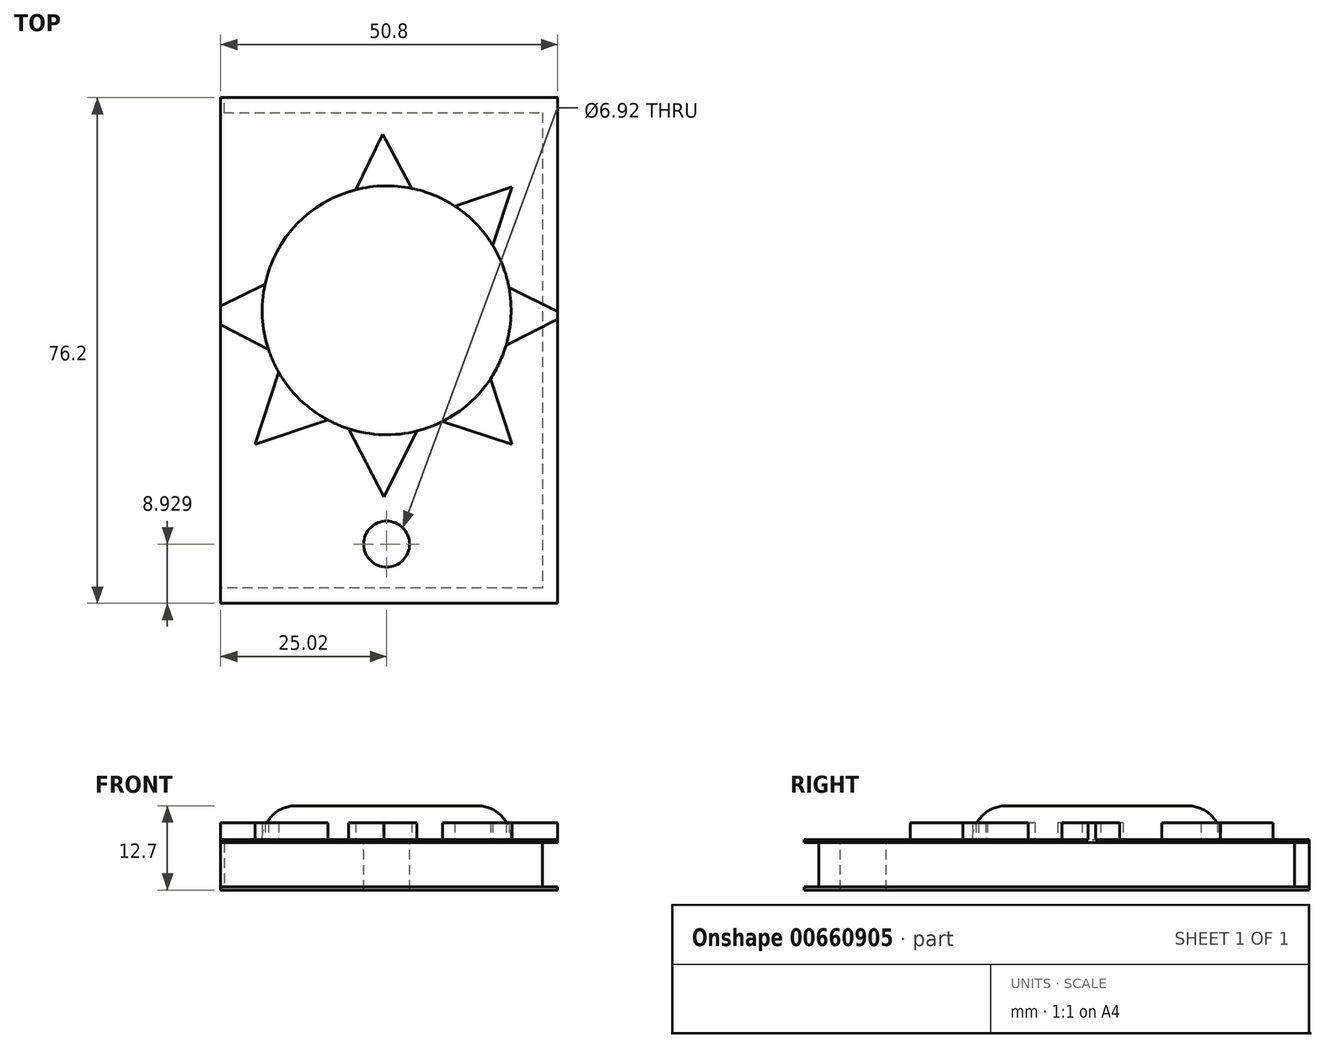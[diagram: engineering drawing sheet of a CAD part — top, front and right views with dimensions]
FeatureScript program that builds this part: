
annotation { "Feature Type Name" : "Feature", "Feature Type Description" : "" }
export const myFeature = defineFeature(function(context is Context, id is Id, definition is map)
    precondition{}
    {
        {
            var Q0;
            Q0=qCreatedBy(makeId("Top.planeOp"),FACE);
            var sketch = newSketch(context, id + "F0", { "sketchPlane" : qUnion([Q0])});
            skLineSegment(sketch, "E0.bottom", {"start": v(-25.02, 32.04) * mm, "end": v(25.78, 32.04) * mm});
            skLineSegment(sketch, "E0.top", {"start": v(-25.02, -44.16) * mm, "end": v(25.78, -44.16) * mm});
            skLineSegment(sketch, "E0.left", {"start": v(-25.02, 32.04) * mm, "end": v(-25.02, -44.16) * mm});
            skLineSegment(sketch, "E0.right", {"start": v(25.78, 32.04) * mm, "end": v(25.78, -44.16) * mm});
            skSolve(sketch);
        }
        {
            var Q0;
            Q0=makeQuery(id+"F0.imprint","IMPRINT",FACE,{"disambiguationData":[TD([[makeQuery(id+"F0.imprint","IMPRINT",EDGE,{"derivedFrom":sQuery(id+"F0.wireOp",EDGE,"E0.bottom")}),-1.0]])]});
            extrude(context, id + "F1", {"entities" : qUnion([Q0]), "depth" : 7.62 * mm, "offsetDistance" : 25.4 * mm});
        }
        {
            var Q0;
            Q0=makeQuery(id+"F1.opExtrude","CAP_FACE",FACE,{"disambiguationData":[OSD([sQuery(id+"F0.wireOp",EDGE,"E0.bottom"),sQuery(id+"F0.wireOp",EDGE,"E0.top"),sQuery(id+"F0.wireOp",EDGE,"E0.left"),sQuery(id+"F0.wireOp",EDGE,"E0.right")])],"isStart":false});
            var sketch = newSketch(context, id + "F2", { "sketchPlane" : qUnion([Q0])});
            skCircle(sketch, "E1", {"center": v(0, 0) * mm, "radius": 18.75 * mm});
            skSolve(sketch);
        }
        {
            var Q0;
            Q0=makeQuery(id+"F2.imprint","IMPRINT",FACE,{"disambiguationData":[TD([[makeQuery(id+"F2.imprint","IMPRINT",EDGE,{"derivedFrom":sQuery(id+"F2.wireOp",EDGE,"E1")}),1.0]])]});
            extrude(context, id + "F3", {"entities" : qUnion([Q0]), "operationType" : NewBodyOperationType.ADD, "depth" : 5.08 * mm, "offsetDistance" : 25.4 * mm});
        }
        {
            var Q0;
            Q0=makeQuery(id+"F3.opExtrude","CAP_EDGE",EDGE,{"disambiguationData":[OSD([sQuery(id+"F2.wireOp",EDGE,"E1")])],"isStart":false});
            fillet(context, id + "F4", {"entities" : qUnion([Q0]), "radius" : 5.08 * mm, "tangentPropagation" : true, "allowEdgeOverflow" : false});
        }
        {
            var Q0;
            Q0=makeQuery(id+"F1.opExtrude","CAP_FACE",FACE,{"disambiguationData":[OSD([sQuery(id+"F0.wireOp",EDGE,"E0.bottom"),sQuery(id+"F0.wireOp",EDGE,"E0.top"),sQuery(id+"F0.wireOp",EDGE,"E0.left"),sQuery(id+"F0.wireOp",EDGE,"E0.right")])],"isStart":false});
            var sketch = newSketch(context, id + "F5", { "sketchPlane" : qUnion([Q0])});
            skLineSegment(sketch, "E2", {"start": v(-16.56, 8.8) * mm, "end": v(-20, 18.6) * mm});
            skLineSegment(sketch, "E3", {"start": v(-20, 18.6) * mm, "end": v(-10.58, 15.49) * mm});
            skLineSegment(sketch, "E4", {"start": v(-10.58, 15.49) * mm, "end": v(-16.56, 8.8) * mm});
            skLineSegment(sketch, "E5", {"start": v(-4.65, 18.17) * mm, "end": v(-0.57, 26.55) * mm});
            skLineSegment(sketch, "E6", {"start": v(-0.57, 26.55) * mm, "end": v(3.77, 18.37) * mm});
            skLineSegment(sketch, "E7", {"start": v(3.77, 18.37) * mm, "end": v(-4.65, 18.17) * mm});
            skLineSegment(sketch, "E8", {"start": v(10.26, 15.7) * mm, "end": v(18.9, 18.59) * mm});
            skLineSegment(sketch, "E9", {"start": v(18.9, 18.59) * mm, "end": v(16, 9.77) * mm});
            skLineSegment(sketch, "E10", {"start": v(16, 9.77) * mm, "end": v(10.26, 15.7) * mm});
            skLineSegment(sketch, "E11", {"start": v(18.43, 3.45) * mm, "end": v(26.88, -0.76) * mm});
            skLineSegment(sketch, "E12", {"start": v(26.88, -0.76) * mm, "end": v(18, -5.29) * mm});
            skLineSegment(sketch, "E13", {"start": v(18, -5.29) * mm, "end": v(18.43, 3.45) * mm});
            skLineSegment(sketch, "E14", {"start": v(8.42, -16.75) * mm, "end": v(18.93, -20.19) * mm});
            skLineSegment(sketch, "E15", {"start": v(18.93, -20.19) * mm, "end": v(15.63, -10.36) * mm});
            skLineSegment(sketch, "E16", {"start": v(15.63, -10.36) * mm, "end": v(8.42, -16.75) * mm});
            skLineSegment(sketch, "E17", {"start": v(4.55, -18.2) * mm, "end": v(-0.38, -28.12) * mm});
            skLineSegment(sketch, "E18", {"start": v(-0.38, -28.12) * mm, "end": v(-5.71, -17.86) * mm});
            skLineSegment(sketch, "E19", {"start": v(-5.71, -17.86) * mm, "end": v(4.55, -18.2) * mm});
            skLineSegment(sketch, "E20", {"start": v(-8.85, -16.53) * mm, "end": v(-19.83, -20.21) * mm});
            skLineSegment(sketch, "E21", {"start": v(-19.83, -20.21) * mm, "end": v(-16.27, -9.32) * mm});
            skLineSegment(sketch, "E22", {"start": v(-16.27, -9.32) * mm, "end": v(-8.85, -16.53) * mm});
            skLineSegment(sketch, "E23", {"start": v(-18.34, 3.93) * mm, "end": v(-27.79, -0.78) * mm});
            skLineSegment(sketch, "E24", {"start": v(-27.79, -0.78) * mm, "end": v(-17.8, -5.9) * mm});
            skLineSegment(sketch, "E25", {"start": v(-17.8, -5.9) * mm, "end": v(-18.34, 3.93) * mm});
            skSolve(sketch);
        }
        {
            var Q0;
            {var subQ0=sQuery(id+"F5.wireOp",EDGE,"E2");Q0=makeQuery(id+"F5.imprint","IMPRINT",FACE,{"disambiguationData":[TD([[makeQuery(id+"F5.imprint","IMPRINT",EDGE,{"derivedFrom":subQ0}),-1.0]])]});}
            var sketch = newSketch(context, id + "F6", { "sketchPlane" : qUnion([Q0])});
            skSolve(sketch);
        }
        {
            var Q0;
            {var subQ1=sQuery(id+"F5.wireOp",EDGE,"E23");var subQ2=sQuery(id+"F0.wireOp",EDGE,"E0.left");var subQ5=makeQuery(id+"F1.opExtrude","CAP_EDGE",EDGE,{"disambiguationData":[OSD([subQ2])],"isStart":false});var subQ6=makeQuery(id+"F5.imprint","INTERSECT",VERTEX,{"derivedFrom":[subQ5,subQ1]});Q0=makeQuery(id+"F5.imprint","IMPRINT",FACE,{"disambiguationData":[TD([[makeQuery(id+"F5.imprint","IMPRINT",EDGE,{"disambiguationData":[TD([[subQ6,-1.0]])],"derivedFrom":subQ5}),1.0]])]});}
            var Q1;
            {var subQ0=sQuery(id+"F5.wireOp",EDGE,"E5");Q1=makeQuery(id+"F5.imprint","IMPRINT",FACE,{"disambiguationData":[TD([[makeQuery(id+"F5.imprint","IMPRINT",EDGE,{"derivedFrom":subQ0}),-1.0]])]});}
            var Q2;
            {var subQ0=sQuery(id+"F5.wireOp",EDGE,"E8");Q2=makeQuery(id+"F5.imprint","IMPRINT",FACE,{"disambiguationData":[TD([[makeQuery(id+"F5.imprint","IMPRINT",EDGE,{"derivedFrom":subQ0}),-1.0]])]});}
            var Q3;
            {var subQ1=sQuery(id+"F5.wireOp",EDGE,"E11");var subQ2=sQuery(id+"F0.wireOp",EDGE,"E0.right");var subQ5=makeQuery(id+"F1.opExtrude","CAP_EDGE",EDGE,{"disambiguationData":[OSD([subQ2])],"isStart":false});var subQ6=makeQuery(id+"F5.imprint","INTERSECT",VERTEX,{"derivedFrom":[subQ5,subQ1]});Q3=makeQuery(id+"F5.imprint","IMPRINT",FACE,{"disambiguationData":[TD([[makeQuery(id+"F5.imprint","IMPRINT",EDGE,{"disambiguationData":[TD([[subQ6,-1.0]])],"derivedFrom":subQ5}),-1.0]])]});}
            var Q4;
            {var subQ0=sQuery(id+"F5.wireOp",EDGE,"E14");Q4=makeQuery(id+"F5.imprint","IMPRINT",FACE,{"disambiguationData":[TD([[makeQuery(id+"F5.imprint","IMPRINT",EDGE,{"derivedFrom":subQ0}),1.0]])]});}
            var Q5;
            {var subQ0=sQuery(id+"F5.wireOp",EDGE,"E17");Q5=makeQuery(id+"F5.imprint","IMPRINT",FACE,{"disambiguationData":[TD([[makeQuery(id+"F5.imprint","IMPRINT",EDGE,{"derivedFrom":subQ0}),-1.0]])]});}
            var Q6;
            {var subQ0=sQuery(id+"F5.wireOp",EDGE,"E20");Q6=makeQuery(id+"F5.imprint","IMPRINT",FACE,{"disambiguationData":[TD([[makeQuery(id+"F5.imprint","IMPRINT",EDGE,{"derivedFrom":subQ0}),-1.0]])]});}
            var Q7;
            {var subQ0=sQuery(id+"F5.wireOp",EDGE,"E2");Q7=makeQuery(id+"F6.imprint","IMPRINT",FACE,{"disambiguationData":[TD([[makeQuery(id+"F6.imprint","IMPRINT",EDGE,{"derivedFrom":makeQuery(id+"F5.imprint","IMPRINT",EDGE,{"derivedFrom":subQ0})}),-1.0]])]});}
            extrude(context, id + "F7", {"entities" : qUnion([Q0, Q1, Q2, Q3, Q4, Q5, Q6, Q7]), "operationType" : NewBodyOperationType.ADD, "depth" : 2.54 * mm, "offsetDistance" : 25.4 * mm});
        }
        {
            var Q0;
            Q0=makeQuery(id+"F1.opExtrude","SWEPT_FACE",FACE,{"disambiguationData":[OSD([sQuery(id+"F0.wireOp",EDGE,"E0.bottom")])]});
            var sketch = newSketch(context, id + "F8", { "sketchPlane" : qUnion([Q0])});
            skLineSegment(sketch, "E26", {"start": v(24.5, 7.13) * mm, "end": v(-25.78, 7.13) * mm});
            skLineSegment(sketch, "E27", {"start": v(24.5, 0.48) * mm, "end": v(-25.78, 0.48) * mm});
            skLineSegment(sketch, "E28", {"start": v(24.5, 7.13) * mm, "end": v(24.5, 0.48) * mm});
            skPoint(sketch, "E29.orphan", {"position": v(25.02, 7.13) * mm});
            skPoint(sketch, "E30.orphan", {"position": v(25.02, 0.48) * mm});
            skSolve(sketch);
        }
        {
            var Q0;
            {var subQ0=sQuery(id+"F8.wireOp",EDGE,"E26");Q0=makeQuery(id+"F8.imprint","IMPRINT",FACE,{"disambiguationData":[TD([[makeQuery(id+"F8.imprint","IMPRINT",EDGE,{"derivedFrom":subQ0}),1.0]])]});}
            extrude(context, id + "F9", {"entities" : qUnion([Q0]), "operationType" : NewBodyOperationType.REMOVE, "oppositeDirection" : true, "depth" : 2.3 * mm, "offsetDistance" : 25.4 * mm});
        }
        {
            var Q0;
            {var subQ0=sQuery(id+"F0.wireOp",EDGE,"E0.right");Q0=makeQuery(id+"F7.boolean.opBoolean","MERGE",FACE,{"derivedFrom":[makeQuery(id+"F1.opExtrude","SWEPT_FACE",FACE,{"disambiguationData":[OSD([subQ0])]}),makeQuery(id+"F7.opExtrude","SWEPT_FACE",FACE,{"disambiguationData":[OSD([subQ0])]})]});}
            var sketch = newSketch(context, id + "F10", { "sketchPlane" : qUnion([Q0])});
            skLineSegment(sketch, "E31", {"start": v(29.76, 7.13) * mm, "end": v(-44.16, 7.13) * mm});
            skPoint(sketch, "E31.endSnap0", {"position": v(-44.16, 3.81) * mm});
            skLineSegment(sketch, "E32", {"start": v(29.76, 0.48) * mm, "end": v(-44.16, 0.48) * mm});
            skSolve(sketch);
        }
        {
            var Q0;
            {var subQ0=sQuery(id+"F10.wireOp",EDGE,"E31");Q0=makeQuery(id+"F10.imprint","IMPRINT",FACE,{"disambiguationData":[TD([[makeQuery(id+"F10.imprint","IMPRINT",EDGE,{"derivedFrom":subQ0}),1.0]])]});}
            extrude(context, id + "F11", {"entities" : qUnion([Q0]), "operationType" : NewBodyOperationType.REMOVE, "oppositeDirection" : true, "depth" : 2.3 * mm, "offsetDistance" : 25.4 * mm});
        }
        {
            var Q0;
            Q0=makeQuery(id+"F1.opExtrude","SWEPT_FACE",FACE,{"disambiguationData":[OSD([sQuery(id+"F0.wireOp",EDGE,"E0.top")])]});
            var sketch = newSketch(context, id + "F12", { "sketchPlane" : qUnion([Q0])});
            skLineSegment(sketch, "E33", {"start": v(23.5, 7.13) * mm, "end": v(-25.02, 7.13) * mm});
            skLineSegment(sketch, "E34", {"start": v(23.5, 0.48) * mm, "end": v(-25.02, 0.48) * mm});
            skSolve(sketch);
        }
        {
            var Q0;
            {var subQ0=sQuery(id+"F12.wireOp",EDGE,"E33");Q0=makeQuery(id+"F12.imprint","IMPRINT",FACE,{"disambiguationData":[TD([[makeQuery(id+"F12.imprint","IMPRINT",EDGE,{"derivedFrom":subQ0}),1.0]])]});}
            extrude(context, id + "F13", {"entities" : qUnion([Q0]), "operationType" : NewBodyOperationType.REMOVE, "oppositeDirection" : true, "depth" : 2.3 * mm, "offsetDistance" : 25.4 * mm});
        }
        {
            var Q0;
            {var subQ5=sQuery(id+"F0.wireOp",EDGE,"E0.right");var subQ6=sQuery(id+"F0.wireOp",EDGE,"E0.left");var subQ7=sQuery(id+"F0.wireOp",EDGE,"E0.top");var subQ8=sQuery(id+"F0.wireOp",EDGE,"E0.bottom");var subQ9=makeQuery(id+"F1.opExtrude","CAP_FACE",FACE,{"disambiguationData":[OSD([subQ8,subQ7,subQ6,subQ5])],"isStart":false});Q0=makeQuery(id+"F7.boolean.opBoolean","SPLIT",FACE,{"disambiguationData":[TD([makeQuery(id+"F1.opExtrude","SWEPT_FACE",FACE,{"disambiguationData":[OSD([subQ7])]})])],"derivedFrom":subQ9});}
            var sketch = newSketch(context, id + "F14", { "sketchPlane" : qUnion([Q0])});
            skCircle(sketch, "E35", {"center": v(0, -35.23) * mm, "radius": 3.46 * mm});
            skSolve(sketch);
        }
        {
            var Q0;
            Q0=makeQuery(id+"F14.imprint","IMPRINT",FACE,{"disambiguationData":[TD([[makeQuery(id+"F14.imprint","IMPRINT",EDGE,{"derivedFrom":sQuery(id+"F14.wireOp",EDGE,"E35")}),1.0]])]});
            extrude(context, id + "F15", {"entities" : qUnion([Q0]), "operationType" : NewBodyOperationType.REMOVE, "oppositeDirection" : true, "depth" : 25.4 * mm, "offsetDistance" : 25.4 * mm});
        }
    });
